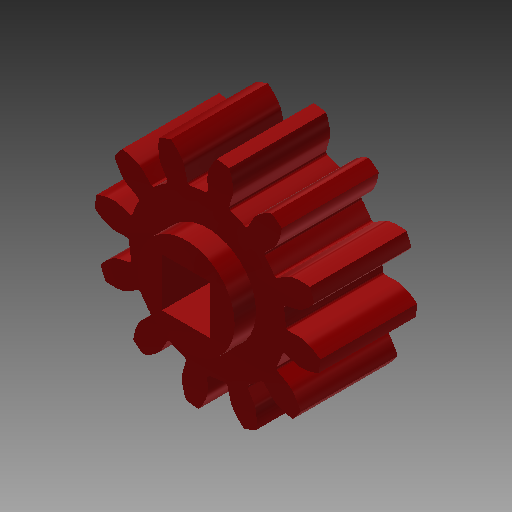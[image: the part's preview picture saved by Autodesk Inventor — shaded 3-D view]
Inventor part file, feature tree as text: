
AUTODESK INVENTOR PART (.ipt)
format: ipt  version: 2018 (Build 220112000, 112)  size: 414,720 bytes
history: native  units: mm (DEFAULTED — no unit token found)
features: imported_body x1, plane x1
ambient origin geometry x8: Origin, YZ Plane, XZ Plane, XY Plane, X Axis, Y Axis, Z Axis, Center Point
bodies: Solid1 (feature_tree)
feature tree (2):
  imported_body  "Base1"
  plane  "Work Plane1"
